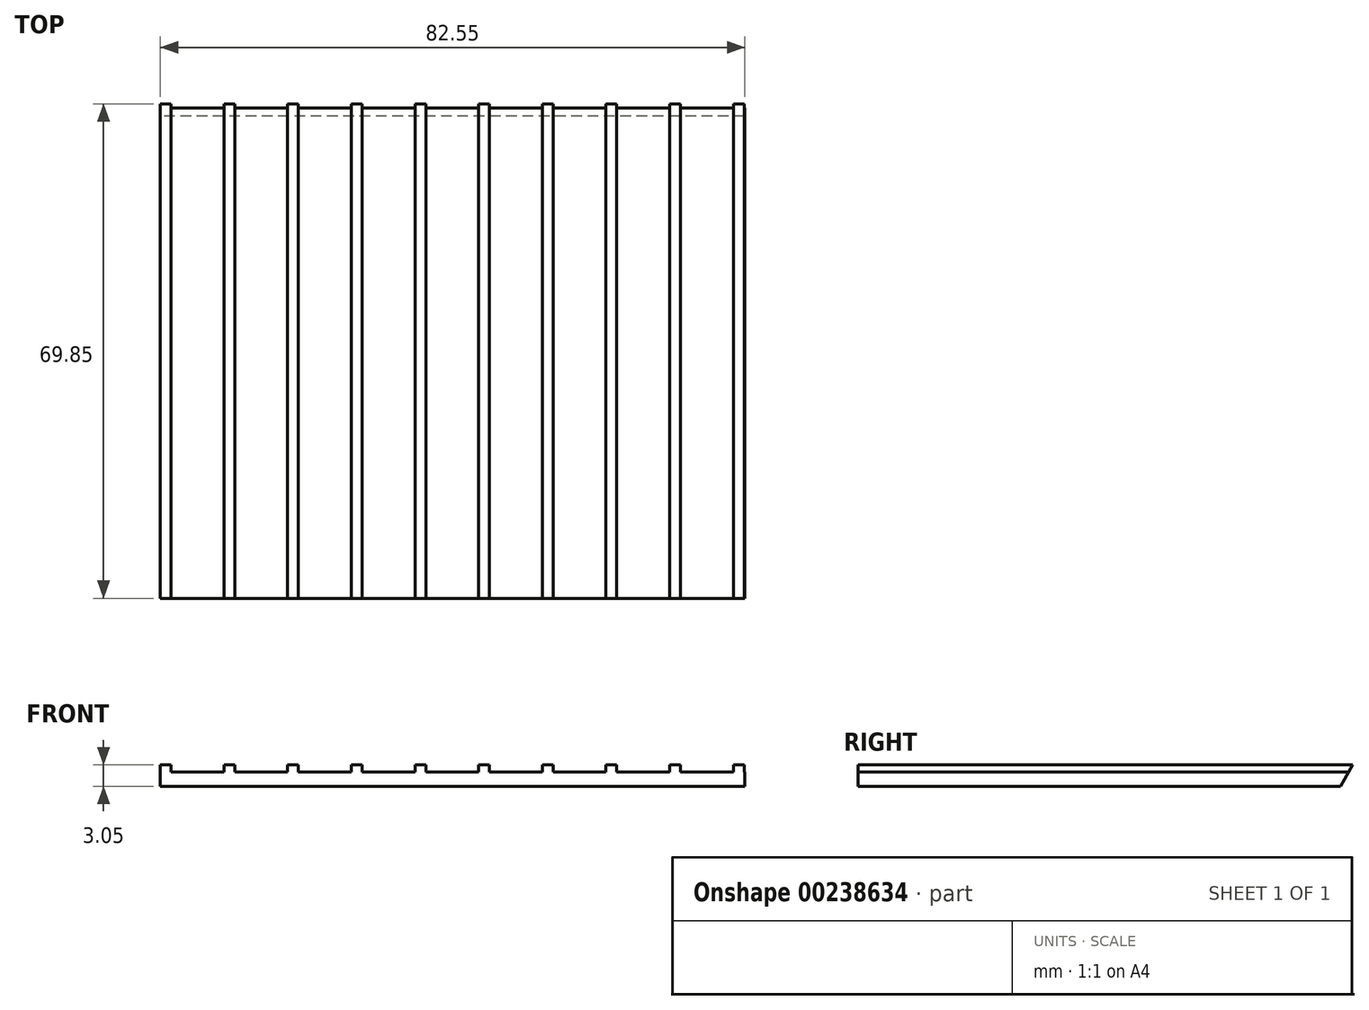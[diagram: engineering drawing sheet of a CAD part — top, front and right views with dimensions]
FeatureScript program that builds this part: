
annotation { "Feature Type Name" : "Feature", "Feature Type Description" : "" }
export const myFeature = defineFeature(function(context is Context, id is Id, definition is map)
    precondition{}
    {
        {
            var Q0;
            Q0=qCreatedBy(makeId("Top.planeOp"),FACE);
            var sketch = newSketch(context, id + "F0", { "sketchPlane" : qUnion([Q0])});
            skLineSegment(sketch, "E0.bottom", {"start": v(-57.3, 35.62) * mm, "end": v(25.26, 35.62) * mm});
            skLineSegment(sketch, "E0.top", {"start": v(-57.3, -34.23) * mm, "end": v(25.26, -34.23) * mm});
            skLineSegment(sketch, "E0.left", {"start": v(-57.3, 35.62) * mm, "end": v(-57.3, -34.23) * mm});
            skLineSegment(sketch, "E0.right", {"start": v(25.26, 35.62) * mm, "end": v(25.26, -34.23) * mm});
            skSolve(sketch);
        }
        {
            var Q0;
            Q0=makeQuery(id+"F0.imprint","IMPRINT",FACE,{"disambiguationData":[TD([[makeQuery(id+"F0.imprint","IMPRINT",EDGE,{"derivedFrom":sQuery(id+"F0.wireOp",EDGE,"E0.bottom")}),-1.0]])]});
            extrude(context, id + "F1", {"entities" : qUnion([Q0]), "depth" : 2.03 * mm});
        }
        {
            var Q0;
            Q0=makeQuery(id+"F1.opExtrude","CAP_FACE",FACE,{"disambiguationData":[OSD([sQuery(id+"F0.wireOp",EDGE,"E0.bottom"),sQuery(id+"F0.wireOp",EDGE,"E0.top"),sQuery(id+"F0.wireOp",EDGE,"E0.left"),sQuery(id+"F0.wireOp",EDGE,"E0.right")])],"isStart":false});
            var sketch = newSketch(context, id + "F2", { "sketchPlane" : qUnion([Q0])});
            skLineSegment(sketch, "E1.bottom", {"start": v(-57.3, 35.62) * mm, "end": v(-55.77, 35.62) * mm});
            skLineSegment(sketch, "E1.top", {"start": v(-57.3, -34.23) * mm, "end": v(-55.77, -34.23) * mm});
            skLineSegment(sketch, "E1.left", {"start": v(-57.3, 35.62) * mm, "end": v(-57.3, -34.23) * mm});
            skLineSegment(sketch, "E1.right", {"start": v(-55.77, 35.62) * mm, "end": v(-55.77, -34.23) * mm});
            skLineSegment(sketch, "E2.1.0.0", {"start": v(-48.3, 35.62) * mm, "end": v(-46.78, 35.62) * mm});
            skLineSegment(sketch, "E2.1.0.1", {"start": v(-48.3, 35.62) * mm, "end": v(-48.3, -34.23) * mm});
            skLineSegment(sketch, "E2.1.0.2", {"start": v(-46.78, 35.62) * mm, "end": v(-46.78, -34.23) * mm});
            skLineSegment(sketch, "E2.1.0.3", {"start": v(-48.3, -34.23) * mm, "end": v(-46.78, -34.23) * mm});
            skLineSegment(sketch, "E2.2.0.0", {"start": v(-39.31, 35.62) * mm, "end": v(-37.79, 35.62) * mm});
            skLineSegment(sketch, "E2.2.0.1", {"start": v(-39.31, 35.62) * mm, "end": v(-39.31, -34.23) * mm});
            skLineSegment(sketch, "E2.2.0.2", {"start": v(-37.79, 35.62) * mm, "end": v(-37.79, -34.23) * mm});
            skLineSegment(sketch, "E2.2.0.3", {"start": v(-39.31, -34.23) * mm, "end": v(-37.79, -34.23) * mm});
            skLineSegment(sketch, "E2.3.0.0", {"start": v(-30.32, 35.62) * mm, "end": v(-28.8, 35.62) * mm});
            skLineSegment(sketch, "E2.3.0.1", {"start": v(-30.32, 35.62) * mm, "end": v(-30.32, -34.23) * mm});
            skLineSegment(sketch, "E2.3.0.2", {"start": v(-28.8, 35.62) * mm, "end": v(-28.8, -34.23) * mm});
            skLineSegment(sketch, "E2.3.0.3", {"start": v(-30.32, -34.23) * mm, "end": v(-28.8, -34.23) * mm});
            skLineSegment(sketch, "E2.4.0.0", {"start": v(-21.33, 35.62) * mm, "end": v(-19.8, 35.62) * mm});
            skLineSegment(sketch, "E2.4.0.1", {"start": v(-21.33, 35.62) * mm, "end": v(-21.33, -34.23) * mm});
            skLineSegment(sketch, "E2.4.0.2", {"start": v(-19.8, 35.62) * mm, "end": v(-19.8, -34.23) * mm});
            skLineSegment(sketch, "E2.4.0.3", {"start": v(-21.33, -34.23) * mm, "end": v(-19.8, -34.23) * mm});
            skLineSegment(sketch, "E2.5.0.0", {"start": v(-12.34, 35.62) * mm, "end": v(-10.81, 35.62) * mm});
            skLineSegment(sketch, "E2.5.0.1", {"start": v(-12.34, 35.62) * mm, "end": v(-12.34, -34.23) * mm});
            skLineSegment(sketch, "E2.5.0.2", {"start": v(-10.81, 35.62) * mm, "end": v(-10.81, -34.23) * mm});
            skLineSegment(sketch, "E2.5.0.3", {"start": v(-12.34, -34.23) * mm, "end": v(-10.81, -34.23) * mm});
            skLineSegment(sketch, "E2.6.0.0", {"start": v(-3.35, 35.62) * mm, "end": v(-1.82, 35.62) * mm});
            skLineSegment(sketch, "E2.6.0.1", {"start": v(-3.35, 35.62) * mm, "end": v(-3.35, -34.23) * mm});
            skLineSegment(sketch, "E2.6.0.2", {"start": v(-1.82, 35.62) * mm, "end": v(-1.82, -34.23) * mm});
            skLineSegment(sketch, "E2.6.0.3", {"start": v(-3.35, -34.23) * mm, "end": v(-1.82, -34.23) * mm});
            skLineSegment(sketch, "E2.7.0.0", {"start": v(5.65, 35.62) * mm, "end": v(7.17, 35.62) * mm});
            skLineSegment(sketch, "E2.7.0.1", {"start": v(5.65, 35.62) * mm, "end": v(5.65, -34.23) * mm});
            skLineSegment(sketch, "E2.7.0.2", {"start": v(7.17, 35.62) * mm, "end": v(7.17, -34.23) * mm});
            skLineSegment(sketch, "E2.7.0.3", {"start": v(5.65, -34.23) * mm, "end": v(7.17, -34.23) * mm});
            skLineSegment(sketch, "E2.8.0.0", {"start": v(14.64, 35.62) * mm, "end": v(16.16, 35.62) * mm});
            skLineSegment(sketch, "E2.8.0.1", {"start": v(14.64, 35.62) * mm, "end": v(14.64, -34.23) * mm});
            skLineSegment(sketch, "E2.8.0.2", {"start": v(16.16, 35.62) * mm, "end": v(16.16, -34.23) * mm});
            skLineSegment(sketch, "E2.8.0.3", {"start": v(14.64, -34.23) * mm, "end": v(16.16, -34.23) * mm});
            skLineSegment(sketch, "E2.9.0.0", {"start": v(23.63, 35.62) * mm, "end": v(25.15, 35.62) * mm});
            skLineSegment(sketch, "E2.9.0.1", {"start": v(23.63, 35.62) * mm, "end": v(23.63, -34.23) * mm});
            skLineSegment(sketch, "E2.9.0.2", {"start": v(25.15, 35.62) * mm, "end": v(25.15, -34.23) * mm});
            skLineSegment(sketch, "E2.9.0.3", {"start": v(23.63, -34.23) * mm, "end": v(25.15, -34.23) * mm});
            skLineSegment(sketch, "E2.direction1", {"start": v(-57.3, 35.62) * mm, "end": v(-48.3, 35.62) * mm, "construction": true});
            skSolve(sketch);
        }
        {
            var Q0;
            Q0=makeQuery(id+"F2.imprint","IMPRINT",FACE,{"disambiguationData":[TD([[makeQuery(id+"F2.imprint","IMPRINT",EDGE,{"derivedFrom":sQuery(id+"F2.wireOp",EDGE,"E1.bottom")}),-1.0]])]});
            var Q1;
            Q1=makeQuery(id+"F2.imprint","IMPRINT",FACE,{"disambiguationData":[TD([[makeQuery(id+"F2.imprint","IMPRINT",EDGE,{"derivedFrom":sQuery(id+"F2.wireOp",EDGE,"E2.1.0.0")}),-1.0]])]});
            var Q2;
            Q2=makeQuery(id+"F2.imprint","IMPRINT",FACE,{"disambiguationData":[TD([[makeQuery(id+"F2.imprint","IMPRINT",EDGE,{"derivedFrom":sQuery(id+"F2.wireOp",EDGE,"E2.2.0.0")}),-1.0]])]});
            var Q3;
            Q3=makeQuery(id+"F2.imprint","IMPRINT",FACE,{"disambiguationData":[TD([[makeQuery(id+"F2.imprint","IMPRINT",EDGE,{"derivedFrom":sQuery(id+"F2.wireOp",EDGE,"E2.3.0.0")}),-1.0]])]});
            var Q4;
            Q4=makeQuery(id+"F2.imprint","IMPRINT",FACE,{"disambiguationData":[TD([[makeQuery(id+"F2.imprint","IMPRINT",EDGE,{"derivedFrom":sQuery(id+"F2.wireOp",EDGE,"E2.4.0.0")}),-1.0]])]});
            var Q5;
            Q5=makeQuery(id+"F2.imprint","IMPRINT",FACE,{"disambiguationData":[TD([[makeQuery(id+"F2.imprint","IMPRINT",EDGE,{"derivedFrom":sQuery(id+"F2.wireOp",EDGE,"E2.5.0.0")}),-1.0]])]});
            var Q6;
            Q6=makeQuery(id+"F2.imprint","IMPRINT",FACE,{"disambiguationData":[TD([[makeQuery(id+"F2.imprint","IMPRINT",EDGE,{"derivedFrom":sQuery(id+"F2.wireOp",EDGE,"E2.6.0.0")}),-1.0]])]});
            var Q7;
            Q7=makeQuery(id+"F2.imprint","IMPRINT",FACE,{"disambiguationData":[TD([[makeQuery(id+"F2.imprint","IMPRINT",EDGE,{"derivedFrom":sQuery(id+"F2.wireOp",EDGE,"E2.7.0.0")}),-1.0]])]});
            var Q8;
            Q8=makeQuery(id+"F2.imprint","IMPRINT",FACE,{"disambiguationData":[TD([[makeQuery(id+"F2.imprint","IMPRINT",EDGE,{"derivedFrom":sQuery(id+"F2.wireOp",EDGE,"E2.8.0.0")}),-1.0]])]});
            var Q9;
            Q9=makeQuery(id+"F2.imprint","IMPRINT",FACE,{"disambiguationData":[TD([[makeQuery(id+"F2.imprint","IMPRINT",EDGE,{"derivedFrom":sQuery(id+"F2.wireOp",EDGE,"E2.9.0.0")}),-1.0]])]});
            extrude(context, id + "F3", {"entities" : qUnion([Q0, Q1, Q2, Q3, Q4, Q5, Q6, Q7, Q8, Q9]), "operationType" : NewBodyOperationType.ADD, "depth" : 1.02 * mm});
        }
        {
            var Q0;
            Q0=makeQuery(id+"F1.opExtrude","SWEPT_FACE",FACE,{"disambiguationData":[OSD([sQuery(id+"F0.wireOp",EDGE,"E0.right")])]});
            var sketch = newSketch(context, id + "F4", { "sketchPlane" : qUnion([Q0])});
            skLineSegment(sketch, "E3", {"start": v(33.7, -0.36) * mm, "end": v(35.67, 3.14) * mm});
            skLineSegment(sketch, "E4", {"start": v(35.67, 3.14) * mm, "end": v(35.67, -0.36) * mm});
            skLineSegment(sketch, "E5", {"start": v(35.67, -0.36) * mm, "end": v(33.7, -0.36) * mm});
            skSolve(sketch);
        }
        {
            var Q0;
            {var subQ0=sQuery(id+"F4.wireOp",EDGE,"E4");Q0=makeQuery(id+"F4.imprint","IMPRINT",FACE,{"disambiguationData":[TD([[makeQuery(id+"F4.imprint","IMPRINT",EDGE,{"derivedFrom":subQ0}),-1.0]])]});}
            var Q1;
            {var subQ1=sQuery(id+"F0.wireOp",EDGE,"E0.right");var subQ6=makeQuery(id+"F1.opExtrude","SWEPT_EDGE",EDGE,{"disambiguationData":[OSD([sQuery(id+"F0.wireOp",EDGE,"E0.bottom"),subQ1])]});Q1=makeQuery(id+"F4.imprint","IMPRINT",FACE,{"disambiguationData":[TD([[makeQuery(id+"F4.imprint","IMPRINT",EDGE,{"derivedFrom":subQ6}),-1.0]])]});}
            extrude(context, id + "F5", {"entities" : qUnion([Q0, Q1]), "operationType" : NewBodyOperationType.REMOVE, "oppositeDirection" : true, "depth" : 88.87 * mm});
        }
    });
